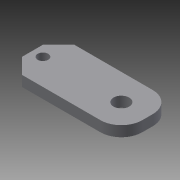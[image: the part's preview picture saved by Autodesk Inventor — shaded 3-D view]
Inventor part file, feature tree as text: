
AUTODESK INVENTOR PART (.ipt)
format: ipt  version: 2013 (Build 170138000, 138)  size: 90,624 bytes
history: native  units: mm
features: extrude x1, fillet x1, chamfer x1, sketch x1
ambient origin geometry x8: Origin, YZ Plane, XZ Plane, XY Plane, X Axis, Y Axis, Z Axis, Center Point
bodies: Solid1 (feature_tree)
feature tree (4):
  extrude  "Extrusion1"  Depth=10.0mm
  fillet  "Fillet1"  Radius=3.0mm
  chamfer  "Chamfer1"  Distance=2.0mm
  sketch  "Sketch1"  dims[d0=22.0mm d1=10.0mm d2=3.0mm d3=2.0mm d4=15.0mm d5=5.0mm d6=2.0mm d7=0.0mm d8=4.0mm d9=3.0mm d10=2.0mm d11=45.0deg]
